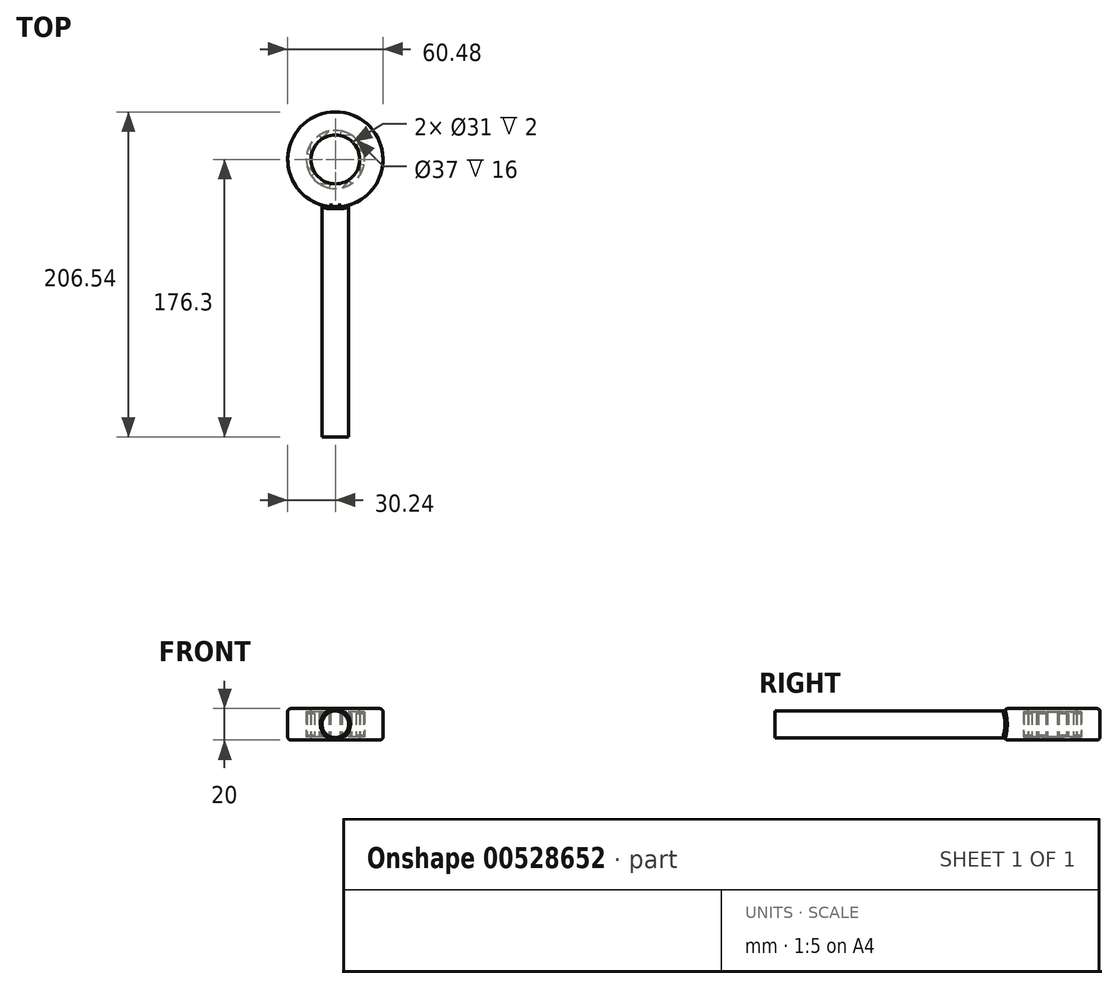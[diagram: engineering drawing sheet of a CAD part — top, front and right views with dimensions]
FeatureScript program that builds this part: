
annotation { "Feature Type Name" : "Feature", "Feature Type Description" : "" }
export const myFeature = defineFeature(function(context is Context, id is Id, definition is map)
    precondition{}
    {
        {
            var Q0;
            Q0=qCreatedBy(makeId("Top.planeOp"),FACE);
            var sketch = newSketch(context, id + "F0", { "sketchPlane" : qUnion([Q0])});
            skCircle(sketch, "E0", {"center": v(0, 0) * mm, "radius": 18.5 * mm});
            skCircle(sketch, "E1", {"center": v(0, 0) * mm, "radius": 30 * mm});
            skSolve(sketch);
        }
        {
            var Q0;
            Q0 = qSketchRegion(id + "F0", true);
            extrude(context, id + "F1", {"entities" : qUnion([Q0]), "depth" : 20 * mm, "offsetDistance" : 25 * mm});
        }
        {
            var Q0;
            Q0=qCreatedBy(makeId("Top.planeOp"),FACE);
            cPlane(context, id + "F2", {"entities" : qUnion([Q0]), "cplaneType" : CPlaneType.OFFSET, "offset" : 10 * mm, "width" : 150 * mm, "height" : 150 * mm});
        }
        {
            var Q0;
            Q0=qCreatedBy(id+"F2.planeOp",FACE);
            var sketch = newSketch(context, id + "F3", { "sketchPlane" : qUnion([Q0])});
            skLineSegment(sketch, "E2.1", {"start": v(18.5, -3.68) * mm, "end": v(15.68, -10.48) * mm});
            skLineSegment(sketch, "E2.3", {"start": v(10.48, -15.68) * mm, "end": v(3.68, -18.5) * mm});
            skLineSegment(sketch, "E2.5", {"start": v(-3.68, -18.5) * mm, "end": v(-10.48, -15.68) * mm});
            skLineSegment(sketch, "E2.7", {"start": v(-15.68, -10.48) * mm, "end": v(-18.5, -3.68) * mm});
            skLineSegment(sketch, "E2.9", {"start": v(-18.5, 3.68) * mm, "end": v(-15.68, 10.48) * mm});
            skLineSegment(sketch, "E2.11", {"start": v(-10.48, 15.68) * mm, "end": v(-3.68, 18.5) * mm});
            skLineSegment(sketch, "E2.13", {"start": v(3.68, 18.5) * mm, "end": v(10.48, 15.68) * mm});
            skLineSegment(sketch, "E2.15", {"start": v(15.68, 10.48) * mm, "end": v(18.5, 3.68) * mm});
            skLineSegment(sketch, "E3", {"start": v(3.68, 18.5) * mm, "end": v(3.1, 15.56) * mm});
            skLineSegment(sketch, "E4", {"start": v(3.1, 15.56) * mm, "end": v(10.48, 15.68) * mm});
            skLineSegment(sketch, "E5", {"start": v(15.68, 10.48) * mm, "end": v(13.19, 8.81) * mm});
            skLineSegment(sketch, "E6", {"start": v(13.19, 8.81) * mm, "end": v(18.5, 3.68) * mm});
            skLineSegment(sketch, "E7", {"start": v(18.5, -3.68) * mm, "end": v(15.56, -3.1) * mm});
            skLineSegment(sketch, "E8", {"start": v(15.56, -3.1) * mm, "end": v(15.68, -10.48) * mm});
            skLineSegment(sketch, "E9", {"start": v(10.48, -15.68) * mm, "end": v(8.81, -13.19) * mm});
            skLineSegment(sketch, "E10", {"start": v(8.81, -13.19) * mm, "end": v(3.68, -18.5) * mm});
            skLineSegment(sketch, "E11", {"start": v(-3.68, -18.5) * mm, "end": v(-3.1, -15.56) * mm});
            skLineSegment(sketch, "E12", {"start": v(-3.1, -15.56) * mm, "end": v(-10.48, -15.68) * mm});
            skLineSegment(sketch, "E13", {"start": v(-15.68, -10.48) * mm, "end": v(-13.19, -8.81) * mm});
            skLineSegment(sketch, "E14", {"start": v(-13.19, -8.81) * mm, "end": v(-18.5, -3.68) * mm});
            skLineSegment(sketch, "E15", {"start": v(-18.5, 3.68) * mm, "end": v(-15.56, 3.1) * mm});
            skLineSegment(sketch, "E16", {"start": v(-15.56, 3.1) * mm, "end": v(-15.68, 10.48) * mm});
            skLineSegment(sketch, "E17", {"start": v(-10.48, 15.68) * mm, "end": v(-8.81, 13.19) * mm});
            skLineSegment(sketch, "E18", {"start": v(-8.81, 13.19) * mm, "end": v(-3.68, 18.5) * mm});
            skSolve(sketch);
        }
        {
            var Q0;
            Q0 = qSketchRegion(id + "F3", true);
            extrude(context, id + "F4", {"entities" : qUnion([Q0]), "operationType" : NewBodyOperationType.ADD, "endBound" : BoundingType.SYMMETRIC, "depth" : 14 * mm, "offsetDistance" : 25 * mm});
        }
        {
            var Q0;
            Q0=qCreatedBy(makeId("Top.planeOp"),FACE);
            var sketch = newSketch(context, id + "F5", { "sketchPlane" : qUnion([Q0])});
            skCircle(sketch, "E19", {"center": v(0, 0) * mm, "radius": 18.5 * mm});
            skCircle(sketch, "E20", {"center": v(0, 0) * mm, "radius": 15.5 * mm});
            skSolve(sketch);
        }
        {
            var Q0;
            Q0=makeQuery(id+"F5.imprint","IMPRINT",FACE,{"disambiguationData":[TD([[makeQuery(id+"F5.imprint","IMPRINT",EDGE,{"derivedFrom":sQuery(id+"F5.wireOp",EDGE,"E19")}),1.0]])]});
            extrude(context, id + "F6", {"entities" : qUnion([Q0]), "operationType" : NewBodyOperationType.ADD, "depth" : 2 * mm, "offsetDistance" : 25 * mm});
        }
        {
            var Q0;
            Q0=makeQuery(id+"F1.opExtrude","CAP_FACE",FACE,{"disambiguationData":[OSD([sQuery(id+"F0.wireOp",EDGE,"E0"),sQuery(id+"F0.wireOp",EDGE,"E1")])],"isStart":false});
            var sketch = newSketch(context, id + "F7", { "sketchPlane" : qUnion([Q0])});
            skCircle(sketch, "E21", {"center": v(0, 0) * mm, "radius": 18.5 * mm});
            skCircle(sketch, "E22", {"center": v(0, 0) * mm, "radius": 15.5 * mm});
            skSolve(sketch);
        }
        {
            var Q0;
            Q0 = qSketchRegion(id + "F7", true);
            extrude(context, id + "F8", {"entities" : qUnion([Q0]), "operationType" : NewBodyOperationType.ADD, "oppositeDirection" : true, "depth" : 2 * mm, "offsetDistance" : 25 * mm});
        }
        {
            var Q0;
            Q0=qCreatedBy(makeId("Top.planeOp"),FACE);
            var sketch = newSketch(context, id + "F9", { "sketchPlane" : qUnion([Q0])});
            skCircle(sketch, "E23", {"center": v(0, 0) * mm, "radius": 30.24 * mm});
            skCircle(sketch, "E24", {"center": v(0, 0) * mm, "radius": 27.64 * mm});
            skSolve(sketch);
        }
        {
            var Q0;
            Q0 = qSketchRegion(id + "F9", true);
            extrude(context, id + "F10", {"entities" : qUnion([Q0]), "operationType" : NewBodyOperationType.ADD, "depth" : 20 * mm, "offsetDistance" : 25 * mm});
        }
        {
            var Q0;
            Q0=qCreatedBy(makeId("Front.planeOp"),FACE);
            cPlane(context, id + "F11", {"entities" : qUnion([Q0]), "cplaneType" : CPlaneType.OFFSET, "offset" : 26.3 * mm, "width" : 150 * mm, "height" : 150 * mm});
        }
        {
            var Q0;
            Q0=qCreatedBy(id+"F11.planeOp",FACE);
            var sketch = newSketch(context, id + "F12", { "sketchPlane" : qUnion([Q0])});
            skCircle(sketch, "E25", {"center": v(0, 10) * mm, "radius": 8.5 * mm});
            skSolve(sketch);
        }
        {
            var Q0;
            Q0 = qSketchRegion(id + "F12", true);
            extrude(context, id + "F13", {"entities" : qUnion([Q0]), "operationType" : NewBodyOperationType.ADD, "depth" : 150 * mm, "offsetDistance" : 25 * mm});
        }
        {
            var Q0;
            Q0=makeQuery(id+"F13.opExtrude","SWEPT_EDGE",EDGE,{"disambiguationData":[OSD([sQuery(id+"F12.wireOp",EDGE,"ViOICCvR-vVvn-mf8R-8bgv-K1lplVGn9t1a.top"),sQuery(id+"F12.wireOp",EDGE,"ViOICCvR-vVvn-mf8R-8bgv-K1lplVGn9t1a.right")])]});
            var Q1;
            Q1=makeQuery(id+"F13.opExtrude","SWEPT_EDGE",EDGE,{"disambiguationData":[OSD([sQuery(id+"F12.wireOp",EDGE,"ViOICCvR-vVvn-mf8R-8bgv-K1lplVGn9t1a.top"),sQuery(id+"F12.wireOp",EDGE,"ViOICCvR-vVvn-mf8R-8bgv-K1lplVGn9t1a.left")])]});
            var Q2;
            Q2=makeQuery(id+"F10.opExtrude","CAP_EDGE",EDGE,{"disambiguationData":[OSD([sQuery(id+"F9.wireOp",EDGE,"5zWzDRIZ-PNAo-oaii-gjcO-1thKee3P4AIe")])],"isStart":false});
            var Q3;
            Q3=makeQuery(id+"F10.opExtrude","CAP_EDGE",EDGE,{"disambiguationData":[OSD([sQuery(id+"F9.wireOp",EDGE,"E23")])],"isStart":false});
            var Q4;
            Q4=makeQuery(id+"F10.opExtrude","CAP_EDGE",EDGE,{"disambiguationData":[OSD([sQuery(id+"F9.wireOp",EDGE,"eb87aeed-f20c-48bf-bd0b-0e7809d42ab40.MirrorCS")])],"isStart":false});
            var Q5;
            Q5=makeQuery(id+"F13.opExtrude","SWEPT_EDGE",EDGE,{"disambiguationData":[OSD([sQuery(id+"F12.wireOp",EDGE,"ViOICCvR-vVvn-mf8R-8bgv-K1lplVGn9t1a.bottom"),sQuery(id+"F12.wireOp",EDGE,"ViOICCvR-vVvn-mf8R-8bgv-K1lplVGn9t1a.right")])]});
            var Q6;
            Q6=makeQuery(id+"F10.opExtrude","CAP_EDGE",EDGE,{"disambiguationData":[OSD([sQuery(id+"F9.wireOp",EDGE,"eb87aeed-f20c-48bf-bd0b-0e7809d42ab40.MirrorCS")])],"isStart":true});
            var Q7;
            Q7=makeQuery(id+"F10.opExtrude","CAP_EDGE",EDGE,{"disambiguationData":[OSD([sQuery(id+"F9.wireOp",EDGE,"E23")])],"isStart":true});
            var Q8;
            Q8=makeQuery(id+"F10.opExtrude","CAP_EDGE",EDGE,{"disambiguationData":[OSD([sQuery(id+"F9.wireOp",EDGE,"5zWzDRIZ-PNAo-oaii-gjcO-1thKee3P4AIe")])],"isStart":true});
            var Q9;
            Q9=makeQuery(id+"F13.opExtrude","SWEPT_EDGE",EDGE,{"disambiguationData":[OSD([sQuery(id+"F12.wireOp",EDGE,"ViOICCvR-vVvn-mf8R-8bgv-K1lplVGn9t1a.bottom"),sQuery(id+"F12.wireOp",EDGE,"ViOICCvR-vVvn-mf8R-8bgv-K1lplVGn9t1a.left")])]});
            fillet(context, id + "F14", {"entities" : qUnion([Q0, Q1, Q2, Q3, Q4, Q5, Q6, Q7, Q8, Q9]), "radius" : 2 * mm, "tangentPropagation" : true, "allowEdgeOverflow" : false});
        }
        {
            var Q0;
            Q0=makeQuery(id+"F13.boolean.opBoolean","INTERSECT",EDGE,{"derivedFrom":[makeQuery(id+"F10.opExtrude","SWEPT_FACE",FACE,{"disambiguationData":[OSD([sQuery(id+"F9.wireOp",EDGE,"E23")])]}),makeQuery(id+"F13.opExtrude","SWEPT_FACE",FACE,{"disambiguationData":[OSD([sQuery(id+"F12.wireOp",EDGE,"E25")])]})]});
            fillet(context, id + "F15", {"entities" : qUnion([Q0]), "radius" : 1.5 * mm, "tangentPropagation" : true, "allowEdgeOverflow" : false});
        }
    });
